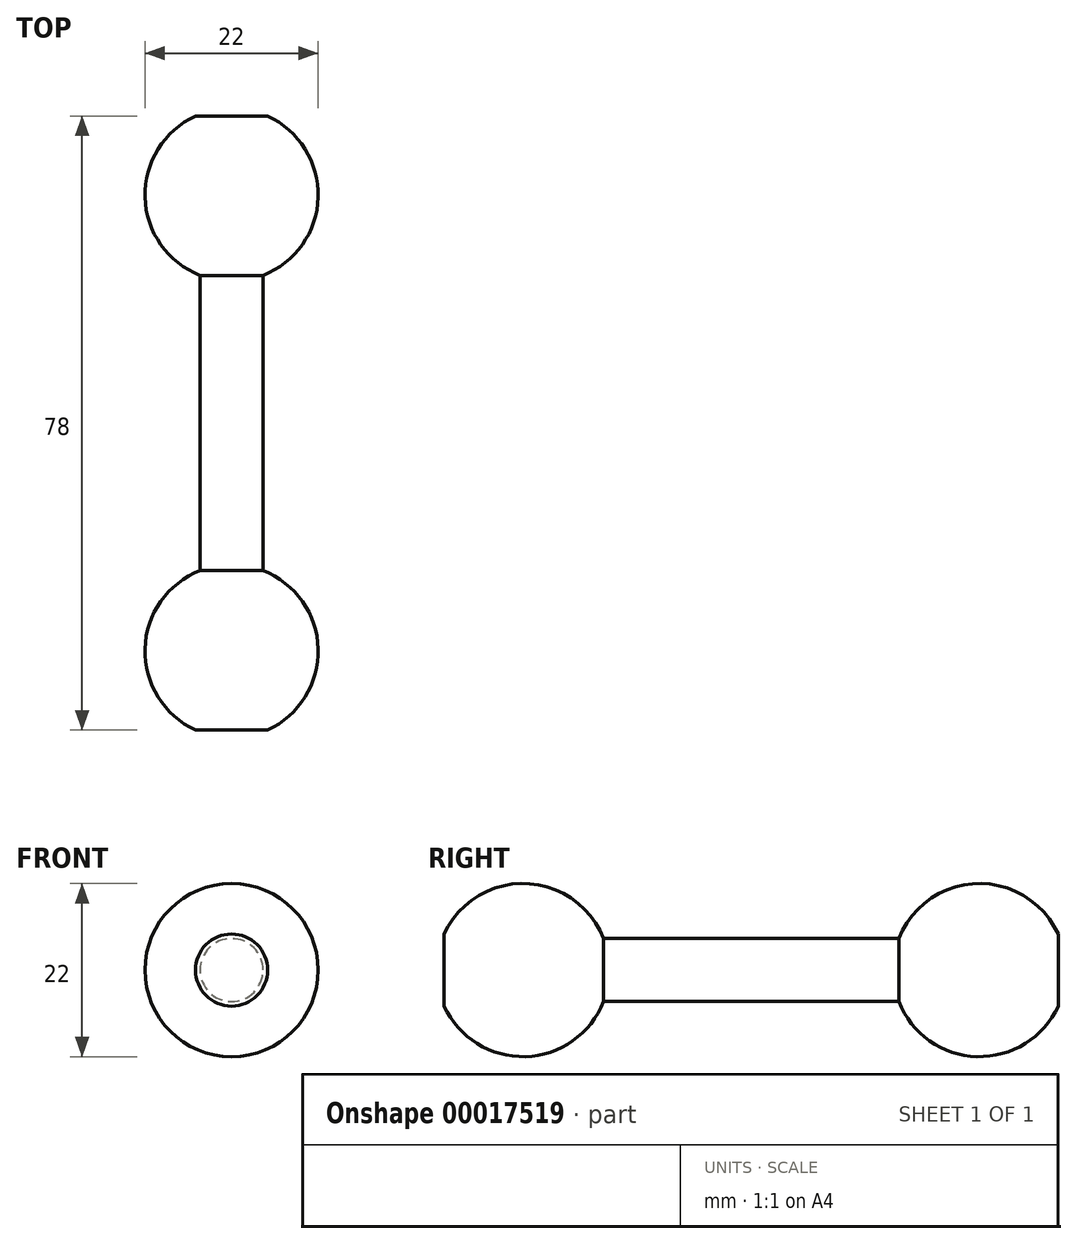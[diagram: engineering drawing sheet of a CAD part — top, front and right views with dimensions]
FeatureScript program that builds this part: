
annotation { "Feature Type Name" : "Feature", "Feature Type Description" : "" }
export const myFeature = defineFeature(function(context is Context, id is Id, definition is map)
    precondition{}
    {
        {
            var Q0;
            Q0=qCreatedBy(makeId("Right.planeOp"),FACE);
            var sketch = newSketch(context, id + "F0", { "sketchPlane" : qUnion([Q0])});
            skLineSegment(sketch, "E0", {"start": v(0, 0) * mm, "end": v(0, 4) * mm});
            skLineSegment(sketch, "E1", {"start": v(0, 4) * mm, "end": v(18.75, 4) * mm});
            skLineSegment(sketch, "E2", {"start": v(40, 4) * mm, "end": v(40, 0) * mm, "construction": true});
            skLineSegment(sketch, "E3", {"start": v(40, 0) * mm, "end": v(0, 0) * mm});
            skLineSegment(sketch, "E4", {"start": v(39, 4.58) * mm, "end": v(39, 0) * mm});
            skArc(sketch, "E5.trimOffspring", {"start": v(39, 4.58) * mm, "mid": v(28.68, 11) * mm, "end": v(18.75, 4) * mm});
            skArc(sketch, "E6", {"start": v(40, 0) * mm, "mid": v(39.75, 2.35) * mm, "end": v(39, 4.58) * mm, "construction": true});
            skSolve(sketch);
        }
        {
            var Q0;
            Q0 = qSketchRegion(id + "F0", true);
            var Q1;
            Q1=sQuery(id+"F0.wireOp",EDGE,"E3");
            revolve(context, id + "F1", {"entities" : qUnion([Q0]), "axis" : qUnion([Q1]), "revolveType" : RevolveType.FULL});
        }
        {
            var Q0;
            Q0=makeQuery(id+"F1.opRevolve","SWEPT_BODY",BODY,{"disambiguationData":[OSD([sQuery(id+"F0.wireOp",EDGE,"E0"),sQuery(id+"F0.wireOp",EDGE,"E1"),sQuery(id+"F0.wireOp",EDGE,"E3"),sQuery(id+"F0.wireOp",EDGE,"E4"),sQuery(id+"F0.wireOp",EDGE,"E5.trimOffspring")])]});
            var Q1;
            Q1=makeQuery(id+"F1.opRevolve","SWEPT_FACE",FACE,{"disambiguationData":[OSD([sQuery(id+"F0.wireOp",EDGE,"E0")])]});
            mirror(context, id + "F2", {"operationType" : NewBodyOperationType.ADD, "entities" : qUnion([Q0]), "mirrorPlane" : qUnion([Q1])});
        }
    });
